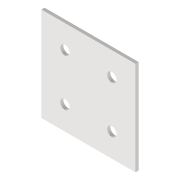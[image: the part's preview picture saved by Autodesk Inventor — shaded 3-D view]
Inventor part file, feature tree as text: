
AUTODESK INVENTOR PART (.ipt)
format: ipt  version: 2022 (Build 260153000, 153)  size: 90,112 bytes
history: native  units: mm
features: extrude x1, sketch x1
ambient origin geometry x8: Origin, YZ Plane, XZ Plane, XY Plane, X Axis, Y Axis, Z Axis, Center Point
bodies: Volumenkörper1 (feature_tree)
feature tree (2):
  extrude  "Extrusion1"  Depth=30.0mm
  sketch  "Skizze1"  dims[d0=30.0mm d1=30.0mm d2=15.0mm d3=15.0mm d4=3.0mm d5=3.0mm d6=3.0mm d7=3.0mm d8=1.0mm d9=0.0mm]
